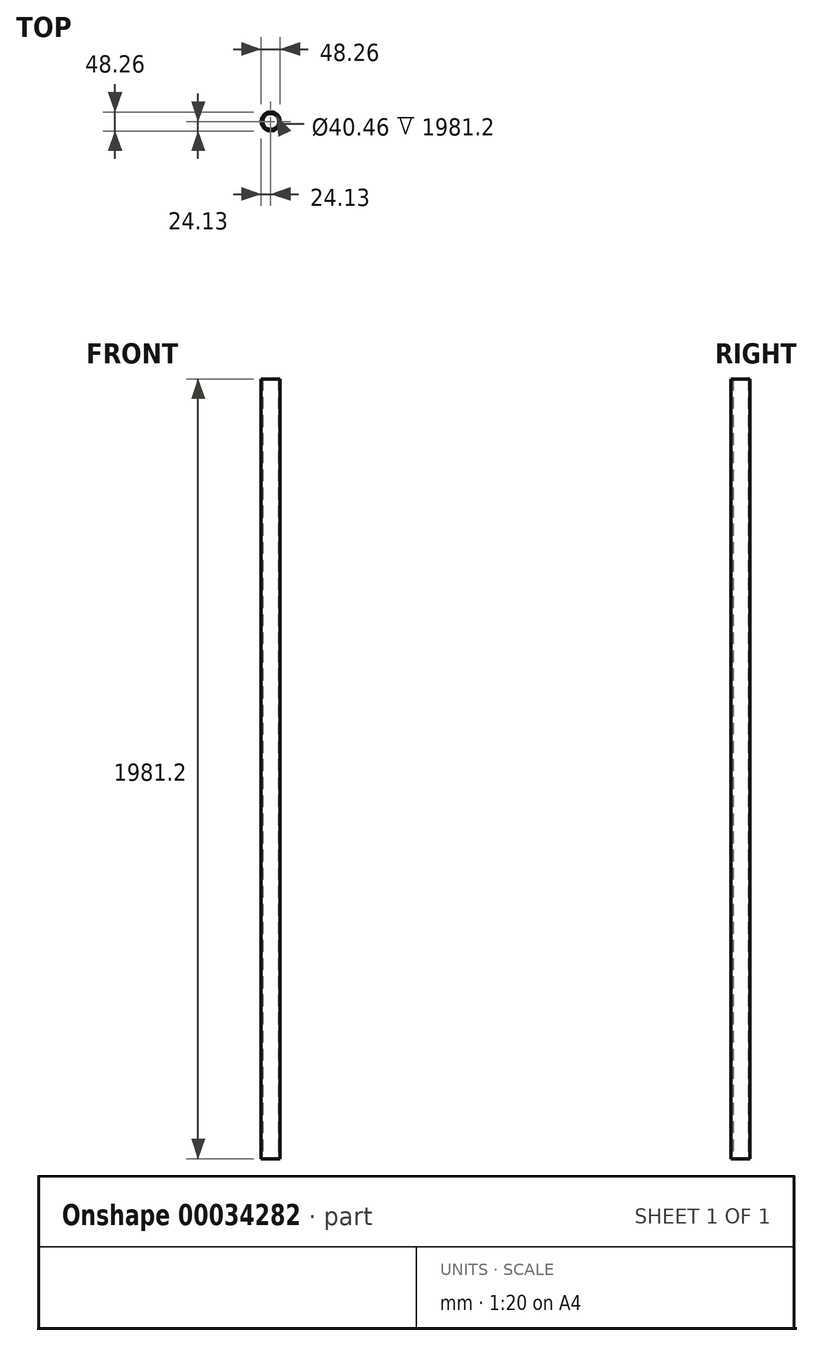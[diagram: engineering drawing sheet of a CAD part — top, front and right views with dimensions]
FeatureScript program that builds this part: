
annotation { "Feature Type Name" : "Feature", "Feature Type Description" : "" }
export const myFeature = defineFeature(function(context is Context, id is Id, definition is map)
    precondition{}
    {
        {
            var Q0;
            Q0=qCreatedBy(makeId("Top.planeOp"),FACE);
            var sketch = newSketch(context, id + "F0", { "sketchPlane" : qUnion([Q0])});
            skCircle(sketch, "E0", {"center": v(0, 0) * mm, "radius": 24.13 * mm});
            skCircle(sketch, "E1", {"center": v(0, 0) * mm, "radius": 20.23 * mm});
            skSolve(sketch);
        }
        {
            var Q0;
            Q0=makeQuery(id+"F0.imprint","IMPRINT",FACE,{"disambiguationData":[TD([[makeQuery(id+"F0.imprint","IMPRINT",EDGE,{"derivedFrom":sQuery(id+"F0.wireOp",EDGE,"E0")}),1.0]])]});
            extrude(context, id + "F1", {"entities" : qUnion([Q0]), "depth" : 1981.2 * mm});
        }
    });
